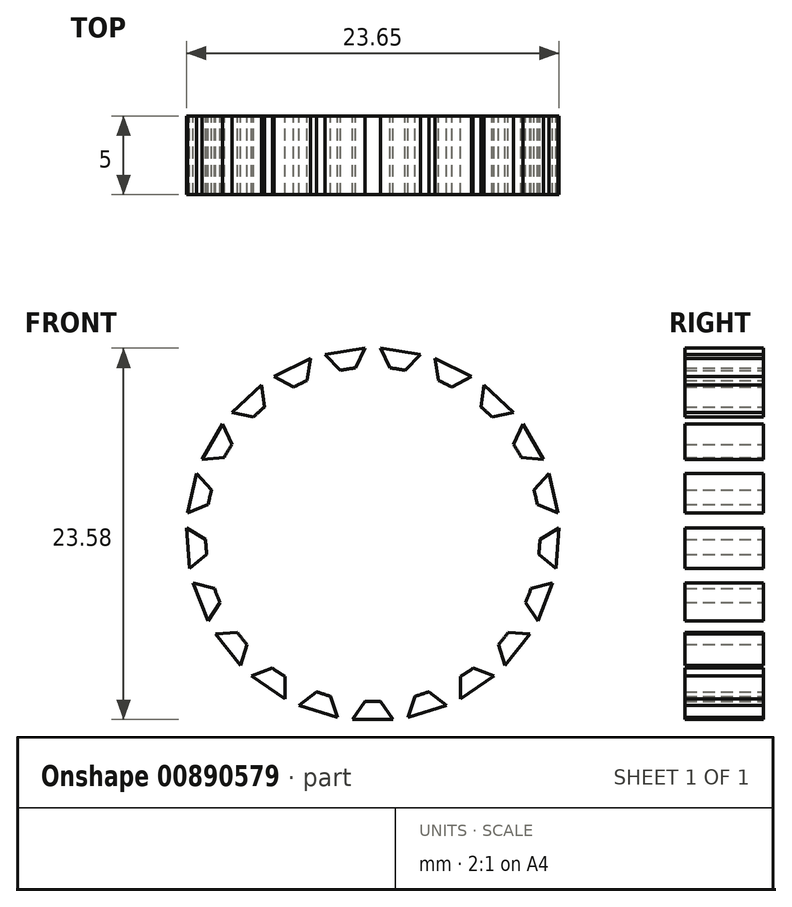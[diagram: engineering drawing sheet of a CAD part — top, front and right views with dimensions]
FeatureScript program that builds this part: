
annotation { "Feature Type Name" : "Feature", "Feature Type Description" : "" }
export const myFeature = defineFeature(function(context is Context, id is Id, definition is map)
    precondition{}
    {
        {
            var Q0;
            Q0=qCreatedBy(makeId("Front.planeOp"),FACE);
            var sketch = newSketch(context, id + "F0", { "sketchPlane" : qUnion([Q0])});
            skLineSegment(sketch, "E0", {"start": v(135.93, 56.36) * mm, "end": v(134.97, 56.36) * mm});
            skPoint(sketch, "E1.visualSharp", {"position": v(134.6, 56.36) * mm});
            skArc(sketch, "E1.filletArc", {"start": v(134.97, 56.36) * mm, "mid": v(134.94, 56.35) * mm, "end": v(134.92, 56.35) * mm});
            skPoint(sketch, "E2.visualSharp", {"position": v(136.3, 56.36) * mm});
            skArc(sketch, "E2.filletArc", {"start": v(135.98, 56.35) * mm, "mid": v(135.96, 56.35) * mm, "end": v(135.93, 56.36) * mm});
            skCircle(sketch, "E3", {"center": v(135.45, 66.96) * mm, "radius": 10.62 * mm});
            skCircle(sketch, "E4", {"center": v(135.45, 66.96) * mm, "radius": 11.83 * mm});
            skPoint(sketch, "E5", {"position": v(135.45, 56.36) * mm});
            skPoint(sketch, "E6", {"position": v(135.45, 77.58) * mm});
            skPoint(sketch, "E7", {"position": v(135.45, 55.2) * mm});
            skLineSegment(sketch, "E8.1.0", {"start": v(140.07, 56.07) * mm, "end": v(139.6, 56.77) * mm});
            skArc(sketch, "E8.1.1", {"start": v(139.6, 56.77) * mm, "mid": v(139.35, 56.96) * mm, "end": v(139.04, 56.97) * mm});
            skLineSegment(sketch, "E8.1.2", {"start": v(139.04, 56.97) * mm, "end": v(138.12, 56.68) * mm});
            skArc(sketch, "E8.1.3", {"start": v(138.12, 56.68) * mm, "mid": v(137.86, 56.5) * mm, "end": v(137.77, 56.2) * mm});
            skLineSegment(sketch, "E8.1.4", {"start": v(137.77, 56.2) * mm, "end": v(137.6, 55.33) * mm});
            skLineSegment(sketch, "E8.2.0", {"start": v(143.07, 57.91) * mm, "end": v(142.42, 58.44) * mm});
            skArc(sketch, "E8.2.1", {"start": v(142.42, 58.44) * mm, "mid": v(142.12, 58.55) * mm, "end": v(141.82, 58.47) * mm});
            skLineSegment(sketch, "E8.2.2", {"start": v(141.82, 58.47) * mm, "end": v(141.03, 57.93) * mm});
            skArc(sketch, "E8.2.3", {"start": v(141.03, 57.93) * mm, "mid": v(140.84, 57.68) * mm, "end": v(140.83, 57.36) * mm});
            skLineSegment(sketch, "E8.2.4", {"start": v(140.83, 57.36) * mm, "end": v(140.93, 56.48) * mm});
            skLineSegment(sketch, "E8.3.0", {"start": v(145.4, 60.56) * mm, "end": v(144.62, 60.87) * mm});
            skArc(sketch, "E8.3.1", {"start": v(144.62, 60.87) * mm, "mid": v(144.3, 60.9) * mm, "end": v(144.04, 60.72) * mm});
            skLineSegment(sketch, "E8.3.2", {"start": v(144.04, 60.72) * mm, "end": v(143.44, 59.97) * mm});
            skArc(sketch, "E8.3.3", {"start": v(143.44, 59.97) * mm, "mid": v(143.33, 59.68) * mm, "end": v(143.42, 59.38) * mm});
            skLineSegment(sketch, "E8.3.4", {"start": v(143.42, 59.38) * mm, "end": v(143.78, 58.56) * mm});
            skLineSegment(sketch, "E8.4.0", {"start": v(146.84, 63.78) * mm, "end": v(146, 63.85) * mm});
            skArc(sketch, "E8.4.1", {"start": v(146, 63.85) * mm, "mid": v(145.7, 63.77) * mm, "end": v(145.5, 63.53) * mm});
            skLineSegment(sketch, "E8.4.2", {"start": v(145.5, 63.53) * mm, "end": v(145.15, 62.64) * mm});
            skArc(sketch, "E8.4.3", {"start": v(145.15, 62.64) * mm, "mid": v(145.13, 62.32) * mm, "end": v(145.3, 62.06) * mm});
            skLineSegment(sketch, "E8.4.4", {"start": v(145.3, 62.06) * mm, "end": v(145.88, 61.4) * mm});
            skLineSegment(sketch, "E8.5.0", {"start": v(147.28, 67.28) * mm, "end": v(146.45, 67.1) * mm});
            skArc(sketch, "E8.5.1", {"start": v(146.45, 67.1) * mm, "mid": v(146.18, 66.94) * mm, "end": v(146.06, 66.65) * mm});
            skLineSegment(sketch, "E8.5.2", {"start": v(146.06, 66.65) * mm, "end": v(145.99, 65.69) * mm});
            skArc(sketch, "E8.5.3", {"start": v(145.99, 65.69) * mm, "mid": v(146.07, 65.38) * mm, "end": v(146.3, 65.18) * mm});
            skLineSegment(sketch, "E8.5.4", {"start": v(146.3, 65.18) * mm, "end": v(147.06, 64.71) * mm});
            skLineSegment(sketch, "E8.6.0", {"start": v(146.66, 70.75) * mm, "end": v(145.92, 70.33) * mm});
            skArc(sketch, "E8.6.1", {"start": v(145.92, 70.33) * mm, "mid": v(145.71, 70.1) * mm, "end": v(145.68, 69.79) * mm});
            skLineSegment(sketch, "E8.6.2", {"start": v(145.68, 69.79) * mm, "end": v(145.9, 68.85) * mm});
            skArc(sketch, "E8.6.3", {"start": v(145.9, 68.85) * mm, "mid": v(146.06, 68.58) * mm, "end": v(146.35, 68.46) * mm});
            skLineSegment(sketch, "E8.6.4", {"start": v(146.35, 68.46) * mm, "end": v(147.2, 68.23) * mm});
            skLineSegment(sketch, "E8.7.0", {"start": v(145.04, 73.88) * mm, "end": v(144.46, 73.27) * mm});
            skArc(sketch, "E8.7.1", {"start": v(144.46, 73.27) * mm, "mid": v(144.33, 72.99) * mm, "end": v(144.4, 72.68) * mm});
            skLineSegment(sketch, "E8.7.2", {"start": v(144.4, 72.68) * mm, "end": v(144.87, 71.85) * mm});
            skArc(sketch, "E8.7.3", {"start": v(144.87, 71.85) * mm, "mid": v(145.1, 71.64) * mm, "end": v(145.42, 71.6) * mm});
            skLineSegment(sketch, "E8.7.4", {"start": v(145.42, 71.6) * mm, "end": v(146.3, 71.64) * mm});
            skLineSegment(sketch, "E8.8.0", {"start": v(142.58, 76.4) * mm, "end": v(142.2, 75.65) * mm});
            skArc(sketch, "E8.8.1", {"start": v(142.2, 75.65) * mm, "mid": v(142.16, 75.33) * mm, "end": v(142.31, 75.06) * mm});
            skLineSegment(sketch, "E8.8.2", {"start": v(142.31, 75.06) * mm, "end": v(143.02, 74.4) * mm});
            skArc(sketch, "E8.8.3", {"start": v(143.02, 74.4) * mm, "mid": v(143.3, 74.28) * mm, "end": v(143.6, 74.34) * mm});
            skLineSegment(sketch, "E8.8.4", {"start": v(143.6, 74.34) * mm, "end": v(144.44, 74.63) * mm});
            skLineSegment(sketch, "E8.9.0", {"start": v(139.48, 78.08) * mm, "end": v(139.34, 77.25) * mm});
            skArc(sketch, "E8.9.1", {"start": v(139.34, 77.25) * mm, "mid": v(139.4, 76.94) * mm, "end": v(139.62, 76.72) * mm});
            skLineSegment(sketch, "E8.9.2", {"start": v(139.62, 76.72) * mm, "end": v(140.48, 76.3) * mm});
            skArc(sketch, "E8.9.3", {"start": v(140.48, 76.3) * mm, "mid": v(140.8, 76.26) * mm, "end": v(141.07, 76.42) * mm});
            skLineSegment(sketch, "E8.9.4", {"start": v(141.07, 76.42) * mm, "end": v(141.78, 76.94) * mm});
            skLineSegment(sketch, "E8.10.0", {"start": v(136.02, 78.78) * mm, "end": v(136.14, 77.94) * mm});
            skArc(sketch, "E8.10.1", {"start": v(136.14, 77.94) * mm, "mid": v(136.28, 77.66) * mm, "end": v(136.56, 77.52) * mm});
            skLineSegment(sketch, "E8.10.2", {"start": v(136.56, 77.52) * mm, "end": v(137.5, 77.37) * mm});
            skArc(sketch, "E8.10.3", {"start": v(137.5, 77.37) * mm, "mid": v(137.82, 77.43) * mm, "end": v(138.03, 77.65) * mm});
            skLineSegment(sketch, "E8.10.4", {"start": v(138.03, 77.65) * mm, "end": v(138.56, 78.37) * mm});
            skLineSegment(sketch, "E8.11.0", {"start": v(132.51, 78.42) * mm, "end": v(132.87, 77.65) * mm});
            skArc(sketch, "E8.11.1", {"start": v(132.87, 77.65) * mm, "mid": v(133.09, 77.43) * mm, "end": v(133.4, 77.37) * mm});
            skLineSegment(sketch, "E8.11.2", {"start": v(133.4, 77.37) * mm, "end": v(134.35, 77.52) * mm});
            skArc(sketch, "E8.11.3", {"start": v(134.35, 77.52) * mm, "mid": v(134.63, 77.66) * mm, "end": v(134.77, 77.94) * mm});
            skLineSegment(sketch, "E8.11.4", {"start": v(134.77, 77.94) * mm, "end": v(135.06, 78.78) * mm});
            skLineSegment(sketch, "E8.12.0", {"start": v(129.26, 77.04) * mm, "end": v(129.83, 76.42) * mm});
            skArc(sketch, "E8.12.1", {"start": v(129.83, 76.42) * mm, "mid": v(130.1, 76.26) * mm, "end": v(130.42, 76.3) * mm});
            skLineSegment(sketch, "E8.12.2", {"start": v(130.42, 76.3) * mm, "end": v(131.28, 76.72) * mm});
            skArc(sketch, "E8.12.3", {"start": v(131.28, 76.72) * mm, "mid": v(131.5, 76.94) * mm, "end": v(131.56, 77.25) * mm});
            skLineSegment(sketch, "E8.12.4", {"start": v(131.56, 77.25) * mm, "end": v(131.6, 78.13) * mm});
            skLineSegment(sketch, "E8.13.0", {"start": v(126.57, 74.77) * mm, "end": v(127.3, 74.34) * mm});
            skArc(sketch, "E8.13.1", {"start": v(127.3, 74.34) * mm, "mid": v(127.6, 74.28) * mm, "end": v(127.89, 74.4) * mm});
            skLineSegment(sketch, "E8.13.2", {"start": v(127.89, 74.4) * mm, "end": v(128.6, 75.06) * mm});
            skArc(sketch, "E8.13.3", {"start": v(128.6, 75.06) * mm, "mid": v(128.74, 75.33) * mm, "end": v(128.7, 75.65) * mm});
            skLineSegment(sketch, "E8.13.4", {"start": v(128.7, 75.65) * mm, "end": v(128.47, 76.5) * mm});
            skLineSegment(sketch, "E8.14.0", {"start": v(124.66, 71.8) * mm, "end": v(125.48, 71.6) * mm});
            skArc(sketch, "E8.14.1", {"start": v(125.48, 71.6) * mm, "mid": v(125.8, 71.64) * mm, "end": v(126.03, 71.85) * mm});
            skLineSegment(sketch, "E8.14.2", {"start": v(126.03, 71.85) * mm, "end": v(126.5, 72.68) * mm});
            skArc(sketch, "E8.14.3", {"start": v(126.5, 72.68) * mm, "mid": v(126.57, 72.99) * mm, "end": v(126.44, 73.27) * mm});
            skLineSegment(sketch, "E8.14.4", {"start": v(126.44, 73.27) * mm, "end": v(125.97, 74.02) * mm});
            skLineSegment(sketch, "E8.15.0", {"start": v(123.7, 68.4) * mm, "end": v(124.55, 68.46) * mm});
            skArc(sketch, "E8.15.1", {"start": v(124.55, 68.46) * mm, "mid": v(124.84, 68.58) * mm, "end": v(125, 68.85) * mm});
            skLineSegment(sketch, "E8.15.2", {"start": v(125, 68.85) * mm, "end": v(125.22, 69.79) * mm});
            skArc(sketch, "E8.15.3", {"start": v(125.22, 69.79) * mm, "mid": v(125.19, 70.1) * mm, "end": v(124.98, 70.33) * mm});
            skLineSegment(sketch, "E8.15.4", {"start": v(124.98, 70.33) * mm, "end": v(124.3, 70.91) * mm});
            skLineSegment(sketch, "E8.16.0", {"start": v(123.8, 64.88) * mm, "end": v(124.6, 65.18) * mm});
            skArc(sketch, "E8.16.1", {"start": v(124.6, 65.18) * mm, "mid": v(124.84, 65.38) * mm, "end": v(124.91, 65.69) * mm});
            skLineSegment(sketch, "E8.16.2", {"start": v(124.91, 65.69) * mm, "end": v(124.84, 66.65) * mm});
            skArc(sketch, "E8.16.3", {"start": v(124.84, 66.65) * mm, "mid": v(124.72, 66.94) * mm, "end": v(124.45, 67.1) * mm});
            skLineSegment(sketch, "E8.16.4", {"start": v(124.45, 67.1) * mm, "end": v(123.64, 67.45) * mm});
            skLineSegment(sketch, "E8.17.0", {"start": v(124.93, 61.54) * mm, "end": v(125.6, 62.06) * mm});
            skArc(sketch, "E8.17.1", {"start": v(125.6, 62.06) * mm, "mid": v(125.77, 62.32) * mm, "end": v(125.76, 62.64) * mm});
            skLineSegment(sketch, "E8.17.2", {"start": v(125.76, 62.64) * mm, "end": v(125.4, 63.53) * mm});
            skArc(sketch, "E8.17.3", {"start": v(125.4, 63.53) * mm, "mid": v(125.2, 63.77) * mm, "end": v(124.9, 63.85) * mm});
            skLineSegment(sketch, "E8.17.4", {"start": v(124.9, 63.85) * mm, "end": v(124.02, 63.95) * mm});
            skLineSegment(sketch, "E8.18.0", {"start": v(127, 58.68) * mm, "end": v(127.48, 59.38) * mm});
            skArc(sketch, "E8.18.1", {"start": v(127.48, 59.38) * mm, "mid": v(127.57, 59.68) * mm, "end": v(127.46, 59.97) * mm});
            skLineSegment(sketch, "E8.18.2", {"start": v(127.46, 59.97) * mm, "end": v(126.86, 60.72) * mm});
            skArc(sketch, "E8.18.3", {"start": v(126.86, 60.72) * mm, "mid": v(126.6, 60.9) * mm, "end": v(126.28, 60.87) * mm});
            skLineSegment(sketch, "E8.18.4", {"start": v(126.28, 60.87) * mm, "end": v(125.41, 60.71) * mm});
            skLineSegment(sketch, "E8.19.0", {"start": v(129.81, 56.56) * mm, "end": v(130.07, 57.36) * mm});
            skArc(sketch, "E8.19.1", {"start": v(130.07, 57.36) * mm, "mid": v(130.07, 57.68) * mm, "end": v(129.87, 57.93) * mm});
            skLineSegment(sketch, "E8.19.2", {"start": v(129.87, 57.93) * mm, "end": v(129.08, 58.47) * mm});
            skArc(sketch, "E8.19.3", {"start": v(129.08, 58.47) * mm, "mid": v(128.78, 58.55) * mm, "end": v(128.48, 58.44) * mm});
            skLineSegment(sketch, "E8.19.4", {"start": v(128.48, 58.44) * mm, "end": v(127.7, 58.03) * mm});
            skLineSegment(sketch, "E8.20.0", {"start": v(133.13, 55.36) * mm, "end": v(133.14, 56.2) * mm});
            skArc(sketch, "E8.20.1", {"start": v(133.14, 56.2) * mm, "mid": v(133.04, 56.5) * mm, "end": v(132.78, 56.68) * mm});
            skLineSegment(sketch, "E8.20.2", {"start": v(132.78, 56.68) * mm, "end": v(131.87, 56.97) * mm});
            skArc(sketch, "E8.20.3", {"start": v(131.87, 56.97) * mm, "mid": v(131.55, 56.96) * mm, "end": v(131.3, 56.77) * mm});
            skLineSegment(sketch, "E8.20.4", {"start": v(131.3, 56.77) * mm, "end": v(130.68, 56.14) * mm});
            skLineSegment(sketch, "E9", {"start": v(134.25, 55.2) * mm, "end": v(134.97, 56.36) * mm});
            skPoint(sketch, "E10.orphan", {"position": v(134.5, 56) * mm});
            skPoint(sketch, "E11.start.orphan", {"position": v(136.65, 55.2) * mm});
            skPoint(sketch, "E12.orphan", {"position": v(136.41, 56) * mm});
            skLineSegment(sketch, "E13", {"start": v(135.98, 56.35) * mm, "end": v(136.65, 55.2) * mm});
            skCircle(sketch, "E14", {"center": v(49.18, 99.28) * mm, "radius": 11.83 * mm});
            skCircle(sketch, "E15", {"center": v(49.18, 99.28) * mm, "radius": 10.62 * mm});
            skLineSegment(sketch, "E16", {"start": v(48.7, 88.67) * mm, "end": v(47.89, 87.52) * mm});
            skLineSegment(sketch, "E17", {"start": v(49.66, 88.67) * mm, "end": v(50.46, 87.52) * mm});
            skLineSegment(sketch, "E18", {"start": v(48.7, 88.67) * mm, "end": v(49.66, 88.67) * mm});
            skLineSegment(sketch, "E19", {"start": v(47.89, 87.52) * mm, "end": v(50.46, 87.52) * mm});
            skPoint(sketch, "E20", {"position": v(49.18, 88.67) * mm});
            skPoint(sketch, "E21", {"position": v(49.18, 87.52) * mm});
            skLineSegment(sketch, "E22.1.0", {"start": v(51.84, 89) * mm, "end": v(52.76, 89.28) * mm});
            skLineSegment(sketch, "E22.1.1", {"start": v(52.76, 89.28) * mm, "end": v(53.87, 88.42) * mm});
            skLineSegment(sketch, "E22.1.2", {"start": v(51.84, 89) * mm, "end": v(51.41, 87.66) * mm});
            skLineSegment(sketch, "E22.1.3", {"start": v(51.41, 87.66) * mm, "end": v(53.87, 88.42) * mm});
            skLineSegment(sketch, "E22.2.0", {"start": v(54.76, 90.24) * mm, "end": v(55.55, 90.78) * mm});
            skLineSegment(sketch, "E22.2.1", {"start": v(55.55, 90.78) * mm, "end": v(56.86, 90.29) * mm});
            skLineSegment(sketch, "E22.2.2", {"start": v(54.76, 90.24) * mm, "end": v(54.74, 88.84) * mm});
            skLineSegment(sketch, "E22.2.3", {"start": v(54.74, 88.84) * mm, "end": v(56.86, 90.29) * mm});
            skLineSegment(sketch, "E22.3.0", {"start": v(57.17, 92.3) * mm, "end": v(57.77, 93.04) * mm});
            skLineSegment(sketch, "E22.3.1", {"start": v(57.77, 93.04) * mm, "end": v(59.17, 92.95) * mm});
            skLineSegment(sketch, "E22.3.2", {"start": v(57.17, 92.3) * mm, "end": v(57.57, 90.94) * mm});
            skLineSegment(sketch, "E22.3.3", {"start": v(57.57, 90.94) * mm, "end": v(59.17, 92.95) * mm});
            skLineSegment(sketch, "E22.4.0", {"start": v(58.88, 94.96) * mm, "end": v(59.23, 95.85) * mm});
            skLineSegment(sketch, "E22.4.1", {"start": v(59.23, 95.85) * mm, "end": v(60.6, 96.18) * mm});
            skLineSegment(sketch, "E22.4.2", {"start": v(58.88, 94.96) * mm, "end": v(59.65, 93.79) * mm});
            skLineSegment(sketch, "E22.4.3", {"start": v(59.65, 93.79) * mm, "end": v(60.6, 96.18) * mm});
            skLineSegment(sketch, "E22.5.0", {"start": v(59.72, 98) * mm, "end": v(59.8, 98.97) * mm});
            skLineSegment(sketch, "E22.5.1", {"start": v(59.8, 98.97) * mm, "end": v(61, 99.68) * mm});
            skLineSegment(sketch, "E22.5.2", {"start": v(59.72, 98) * mm, "end": v(60.8, 97.12) * mm});
            skLineSegment(sketch, "E22.5.3", {"start": v(60.8, 97.12) * mm, "end": v(61, 99.68) * mm});
            skLineSegment(sketch, "E22.6.0", {"start": v(59.63, 101.17) * mm, "end": v(59.41, 102.1) * mm});
            skLineSegment(sketch, "E22.6.1", {"start": v(59.41, 102.1) * mm, "end": v(60.35, 103.15) * mm});
            skLineSegment(sketch, "E22.6.2", {"start": v(59.63, 101.17) * mm, "end": v(60.93, 100.64) * mm});
            skLineSegment(sketch, "E22.6.3", {"start": v(60.93, 100.64) * mm, "end": v(60.35, 103.15) * mm});
            skLineSegment(sketch, "E22.7.0", {"start": v(58.6, 104.17) * mm, "end": v(58.12, 105) * mm});
            skLineSegment(sketch, "E22.7.1", {"start": v(58.12, 105) * mm, "end": v(58.72, 106.27) * mm});
            skLineSegment(sketch, "E22.7.2", {"start": v(58.6, 104.17) * mm, "end": v(60, 104.05) * mm});
            skLineSegment(sketch, "E22.7.3", {"start": v(60, 104.05) * mm, "end": v(58.72, 106.27) * mm});
            skLineSegment(sketch, "E22.8.0", {"start": v(56.74, 106.73) * mm, "end": v(56.04, 107.38) * mm});
            skLineSegment(sketch, "E22.8.1", {"start": v(56.04, 107.38) * mm, "end": v(56.23, 108.78) * mm});
            skLineSegment(sketch, "E22.8.2", {"start": v(56.74, 106.73) * mm, "end": v(58.12, 107.03) * mm});
            skLineSegment(sketch, "E22.8.3", {"start": v(58.12, 107.03) * mm, "end": v(56.23, 108.78) * mm});
            skLineSegment(sketch, "E22.9.0", {"start": v(54.21, 108.63) * mm, "end": v(53.35, 109.05) * mm});
            skLineSegment(sketch, "E22.9.1", {"start": v(53.35, 109.05) * mm, "end": v(53.12, 110.43) * mm});
            skLineSegment(sketch, "E22.9.2", {"start": v(54.21, 108.63) * mm, "end": v(55.44, 109.32) * mm});
            skLineSegment(sketch, "E22.9.3", {"start": v(55.44, 109.32) * mm, "end": v(53.12, 110.43) * mm});
            skLineSegment(sketch, "E22.10.0", {"start": v(51.23, 109.7) * mm, "end": v(50.28, 109.84) * mm});
            skLineSegment(sketch, "E22.10.1", {"start": v(50.28, 109.84) * mm, "end": v(49.66, 111.1) * mm});
            skLineSegment(sketch, "E22.10.2", {"start": v(51.23, 109.7) * mm, "end": v(52.2, 110.72) * mm});
            skLineSegment(sketch, "E22.10.3", {"start": v(52.2, 110.72) * mm, "end": v(49.66, 111.1) * mm});
            skLineSegment(sketch, "E22.11.0", {"start": v(48.07, 109.84) * mm, "end": v(47.12, 109.7) * mm});
            skLineSegment(sketch, "E22.11.1", {"start": v(47.12, 109.7) * mm, "end": v(46.15, 110.72) * mm});
            skLineSegment(sketch, "E22.11.2", {"start": v(48.07, 109.84) * mm, "end": v(48.7, 111.1) * mm});
            skLineSegment(sketch, "E22.11.3", {"start": v(48.7, 111.1) * mm, "end": v(46.15, 110.72) * mm});
            skLineSegment(sketch, "E22.12.0", {"start": v(45, 109.05) * mm, "end": v(44.14, 108.63) * mm});
            skLineSegment(sketch, "E22.12.1", {"start": v(44.14, 108.63) * mm, "end": v(42.91, 109.32) * mm});
            skLineSegment(sketch, "E22.12.2", {"start": v(45, 109.05) * mm, "end": v(45.23, 110.43) * mm});
            skLineSegment(sketch, "E22.12.3", {"start": v(45.23, 110.43) * mm, "end": v(42.91, 109.32) * mm});
            skLineSegment(sketch, "E22.13.0", {"start": v(42.31, 107.38) * mm, "end": v(41.6, 106.73) * mm});
            skLineSegment(sketch, "E22.13.1", {"start": v(41.6, 106.73) * mm, "end": v(40.23, 107.03) * mm});
            skLineSegment(sketch, "E22.13.2", {"start": v(42.31, 107.38) * mm, "end": v(42.12, 108.78) * mm});
            skLineSegment(sketch, "E22.13.3", {"start": v(42.12, 108.78) * mm, "end": v(40.23, 107.03) * mm});
            skLineSegment(sketch, "E22.14.0", {"start": v(40.23, 105) * mm, "end": v(39.75, 104.17) * mm});
            skLineSegment(sketch, "E22.14.1", {"start": v(39.75, 104.17) * mm, "end": v(38.35, 104.05) * mm});
            skLineSegment(sketch, "E22.14.2", {"start": v(40.23, 105) * mm, "end": v(39.63, 106.27) * mm});
            skLineSegment(sketch, "E22.14.3", {"start": v(39.63, 106.27) * mm, "end": v(38.35, 104.05) * mm});
            skLineSegment(sketch, "E22.15.0", {"start": v(38.94, 102.1) * mm, "end": v(38.73, 101.17) * mm});
            skLineSegment(sketch, "E22.15.1", {"start": v(38.73, 101.17) * mm, "end": v(37.42, 100.64) * mm});
            skLineSegment(sketch, "E22.15.2", {"start": v(38.94, 102.1) * mm, "end": v(38, 103.15) * mm});
            skLineSegment(sketch, "E22.15.3", {"start": v(38, 103.15) * mm, "end": v(37.42, 100.64) * mm});
            skLineSegment(sketch, "E22.16.0", {"start": v(38.56, 98.97) * mm, "end": v(38.63, 98) * mm});
            skLineSegment(sketch, "E22.16.1", {"start": v(38.63, 98) * mm, "end": v(37.54, 97.12) * mm});
            skLineSegment(sketch, "E22.16.2", {"start": v(38.56, 98.97) * mm, "end": v(37.35, 99.68) * mm});
            skLineSegment(sketch, "E22.16.3", {"start": v(37.35, 99.68) * mm, "end": v(37.54, 97.12) * mm});
            skLineSegment(sketch, "E22.17.0", {"start": v(39.12, 95.85) * mm, "end": v(39.47, 94.96) * mm});
            skLineSegment(sketch, "E22.17.1", {"start": v(39.47, 94.96) * mm, "end": v(38.7, 93.79) * mm});
            skLineSegment(sketch, "E22.17.2", {"start": v(39.12, 95.85) * mm, "end": v(37.76, 96.18) * mm});
            skLineSegment(sketch, "E22.17.3", {"start": v(37.76, 96.18) * mm, "end": v(38.7, 93.79) * mm});
            skLineSegment(sketch, "E22.18.0", {"start": v(40.58, 93.04) * mm, "end": v(41.18, 92.3) * mm});
            skLineSegment(sketch, "E22.18.1", {"start": v(41.18, 92.3) * mm, "end": v(40.78, 90.94) * mm});
            skLineSegment(sketch, "E22.18.2", {"start": v(40.58, 93.04) * mm, "end": v(39.18, 92.95) * mm});
            skLineSegment(sketch, "E22.18.3", {"start": v(39.18, 92.95) * mm, "end": v(40.78, 90.94) * mm});
            skLineSegment(sketch, "E22.19.0", {"start": v(42.8, 90.78) * mm, "end": v(43.6, 90.24) * mm});
            skLineSegment(sketch, "E22.19.1", {"start": v(43.6, 90.24) * mm, "end": v(43.61, 88.84) * mm});
            skLineSegment(sketch, "E22.19.2", {"start": v(42.8, 90.78) * mm, "end": v(41.49, 90.29) * mm});
            skLineSegment(sketch, "E22.19.3", {"start": v(41.49, 90.29) * mm, "end": v(43.61, 88.84) * mm});
            skLineSegment(sketch, "E22.20.0", {"start": v(45.59, 89.28) * mm, "end": v(46.5, 89) * mm});
            skLineSegment(sketch, "E22.20.1", {"start": v(46.5, 89) * mm, "end": v(46.94, 87.66) * mm});
            skLineSegment(sketch, "E22.20.2", {"start": v(45.59, 89.28) * mm, "end": v(44.48, 88.42) * mm});
            skLineSegment(sketch, "E22.20.3", {"start": v(44.48, 88.42) * mm, "end": v(46.94, 87.66) * mm});
            skSolve(sketch);
        }
        {
            var Q0;
            {var subQ3=sQuery(id+"F0.wireOp",EDGE,"E22.20.1");Q0=makeQuery(id+"F0.imprint","IMPRINT",FACE,{"disambiguationData":[TD([[makeQuery(id+"F0.imprint","IMPRINT",EDGE,{"derivedFrom":subQ3}),-1.0]])]});}
            var Q1;
            {var subQ3=sQuery(id+"F0.wireOp",EDGE,"E22.19.1");Q1=makeQuery(id+"F0.imprint","IMPRINT",FACE,{"disambiguationData":[TD([[makeQuery(id+"F0.imprint","IMPRINT",EDGE,{"derivedFrom":subQ3}),-1.0]])]});}
            var Q2;
            {var subQ3=sQuery(id+"F0.wireOp",EDGE,"E22.18.1");Q2=makeQuery(id+"F0.imprint","IMPRINT",FACE,{"disambiguationData":[TD([[makeQuery(id+"F0.imprint","IMPRINT",EDGE,{"derivedFrom":subQ3}),-1.0]])]});}
            var Q3;
            {var subQ3=sQuery(id+"F0.wireOp",EDGE,"E22.17.1");Q3=makeQuery(id+"F0.imprint","IMPRINT",FACE,{"disambiguationData":[TD([[makeQuery(id+"F0.imprint","IMPRINT",EDGE,{"derivedFrom":subQ3}),-1.0]])]});}
            var Q4;
            {var subQ3=sQuery(id+"F0.wireOp",EDGE,"E22.16.1");Q4=makeQuery(id+"F0.imprint","IMPRINT",FACE,{"disambiguationData":[TD([[makeQuery(id+"F0.imprint","IMPRINT",EDGE,{"derivedFrom":subQ3}),-1.0]])]});}
            var Q5;
            {var subQ3=sQuery(id+"F0.wireOp",EDGE,"E22.15.1");Q5=makeQuery(id+"F0.imprint","IMPRINT",FACE,{"disambiguationData":[TD([[makeQuery(id+"F0.imprint","IMPRINT",EDGE,{"derivedFrom":subQ3}),-1.0]])]});}
            var Q6;
            {var subQ3=sQuery(id+"F0.wireOp",EDGE,"E22.14.1");Q6=makeQuery(id+"F0.imprint","IMPRINT",FACE,{"disambiguationData":[TD([[makeQuery(id+"F0.imprint","IMPRINT",EDGE,{"derivedFrom":subQ3}),-1.0]])]});}
            var Q7;
            {var subQ1=sQuery(id+"F0.wireOp",EDGE,"E16");Q7=makeQuery(id+"F0.imprint","IMPRINT",FACE,{"disambiguationData":[TD([[makeQuery(id+"F0.imprint","IMPRINT",EDGE,{"derivedFrom":subQ1}),1.0]])]});}
            var Q8;
            {var subQ3=sQuery(id+"F0.wireOp",EDGE,"E22.1.1");Q8=makeQuery(id+"F0.imprint","IMPRINT",FACE,{"disambiguationData":[TD([[makeQuery(id+"F0.imprint","IMPRINT",EDGE,{"derivedFrom":subQ3}),-1.0]])]});}
            var Q9;
            {var subQ3=sQuery(id+"F0.wireOp",EDGE,"E22.2.1");Q9=makeQuery(id+"F0.imprint","IMPRINT",FACE,{"disambiguationData":[TD([[makeQuery(id+"F0.imprint","IMPRINT",EDGE,{"derivedFrom":subQ3}),-1.0]])]});}
            var Q10;
            {var subQ3=sQuery(id+"F0.wireOp",EDGE,"E22.3.1");Q10=makeQuery(id+"F0.imprint","IMPRINT",FACE,{"disambiguationData":[TD([[makeQuery(id+"F0.imprint","IMPRINT",EDGE,{"derivedFrom":subQ3}),-1.0]])]});}
            var Q11;
            {var subQ3=sQuery(id+"F0.wireOp",EDGE,"E22.4.1");Q11=makeQuery(id+"F0.imprint","IMPRINT",FACE,{"disambiguationData":[TD([[makeQuery(id+"F0.imprint","IMPRINT",EDGE,{"derivedFrom":subQ3}),-1.0]])]});}
            var Q12;
            {var subQ3=sQuery(id+"F0.wireOp",EDGE,"E22.5.1");Q12=makeQuery(id+"F0.imprint","IMPRINT",FACE,{"disambiguationData":[TD([[makeQuery(id+"F0.imprint","IMPRINT",EDGE,{"derivedFrom":subQ3}),-1.0]])]});}
            var Q13;
            {var subQ3=sQuery(id+"F0.wireOp",EDGE,"E22.6.1");Q13=makeQuery(id+"F0.imprint","IMPRINT",FACE,{"disambiguationData":[TD([[makeQuery(id+"F0.imprint","IMPRINT",EDGE,{"derivedFrom":subQ3}),-1.0]])]});}
            var Q14;
            {var subQ3=sQuery(id+"F0.wireOp",EDGE,"E22.7.1");Q14=makeQuery(id+"F0.imprint","IMPRINT",FACE,{"disambiguationData":[TD([[makeQuery(id+"F0.imprint","IMPRINT",EDGE,{"derivedFrom":subQ3}),-1.0]])]});}
            var Q15;
            {var subQ3=sQuery(id+"F0.wireOp",EDGE,"E22.8.1");Q15=makeQuery(id+"F0.imprint","IMPRINT",FACE,{"disambiguationData":[TD([[makeQuery(id+"F0.imprint","IMPRINT",EDGE,{"derivedFrom":subQ3}),-1.0]])]});}
            var Q16;
            {var subQ3=sQuery(id+"F0.wireOp",EDGE,"E22.9.1");Q16=makeQuery(id+"F0.imprint","IMPRINT",FACE,{"disambiguationData":[TD([[makeQuery(id+"F0.imprint","IMPRINT",EDGE,{"derivedFrom":subQ3}),-1.0]])]});}
            var Q17;
            {var subQ3=sQuery(id+"F0.wireOp",EDGE,"E22.10.1");Q17=makeQuery(id+"F0.imprint","IMPRINT",FACE,{"disambiguationData":[TD([[makeQuery(id+"F0.imprint","IMPRINT",EDGE,{"derivedFrom":subQ3}),-1.0]])]});}
            var Q18;
            {var subQ3=sQuery(id+"F0.wireOp",EDGE,"E22.13.1");Q18=makeQuery(id+"F0.imprint","IMPRINT",FACE,{"disambiguationData":[TD([[makeQuery(id+"F0.imprint","IMPRINT",EDGE,{"derivedFrom":subQ3}),-1.0]])]});}
            var Q19;
            {var subQ3=sQuery(id+"F0.wireOp",EDGE,"E22.12.1");Q19=makeQuery(id+"F0.imprint","IMPRINT",FACE,{"disambiguationData":[TD([[makeQuery(id+"F0.imprint","IMPRINT",EDGE,{"derivedFrom":subQ3}),-1.0]])]});}
            var Q20;
            {var subQ3=sQuery(id+"F0.wireOp",EDGE,"E22.11.1");Q20=makeQuery(id+"F0.imprint","IMPRINT",FACE,{"disambiguationData":[TD([[makeQuery(id+"F0.imprint","IMPRINT",EDGE,{"derivedFrom":subQ3}),-1.0]])]});}
            extrude(context, id + "F1", {"entities" : qUnion([Q0, Q1, Q2, Q3, Q4, Q5, Q6, Q7, Q8, Q9, Q10, Q11, Q12, Q13, Q14, Q15, Q16, Q17, Q18, Q19, Q20]), "depth" : 5 * mm, "offsetDistance" : 25 * mm});
        }
    });
